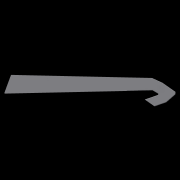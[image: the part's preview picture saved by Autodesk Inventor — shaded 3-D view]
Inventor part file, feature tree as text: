
AUTODESK INVENTOR PART (.ipt)
format: ipt  version: 2020 (Build 240168000, 168)  size: 9,527,808 bytes
history: native  units: in
note: dims shown in document units (in); Inventor stores cm internally (conversion verified against a paired STEP export)
features: other x166, extrude x71, fillet x44, projected_geometry x9, sketch x6, hole x4, loft x3, reference x2, plane x1, move_body x1
ambient origin geometry x8: Origin, YZ Plane, XZ Plane, XY Plane, X Axis, Y Axis, Z Axis, Center Point
bodies: Body (feature_tree), BodyFeature (feature_tree), BodyCut (feature_tree), BodyCutFeature (feature_tree), BodyCutFilletFeature (feature_tree), BodyCutCombineFeature (feature_tree), BodyCutEdgeFilletFeature (feature_tree), BodyRibFrontFilletsFeature (feature_tree), BodyBackRibFilletsFeature (feature_tree), BodyFretboardFilletsFeature (feature_tree), BodyFrontTopFilletsFeature (feature_tree), BodyFrontBottomFilletsFeature (feature_tree), BodyFrontNeckFilletsFeature (feature_tree), Solid22 (feature_tree), Solid23 (feature_tree), Solid62 (feature_tree), Solid64 (feature_tree), Solid65 (feature_tree), Solid68 (feature_tree), Solid50 (feature_tree), Solid52 (feature_tree), Solid54 (feature_tree), Solid56 (feature_tree), Solid57 (feature_tree), Solid59 (feature_tree)
feature tree (307):
  other  "MainBody"
  extrude  "NeckMountsProfileFeature"  Depth=0.5in TaperAngle=0.0deg
  other  "NeckPlane"
  extrude  "8StringFeature"  Depth=4.5in
  extrude  "6StringFeature"  Depth=1.12in
  extrude  "HornFeature"  Depth=0.6788in
  other  "6StringNeckFeature"
  other  "8StringNeckFeature"
  fillet  "InsideCornerFilletsFeature1/8"  Radius=0.6788in
  fillet  "OutsideFilletsFeature1/2"  Radius=0.125in
  fillet  "NeckMountOutsideFilletsFeature1/4"  Radius=0.5in
  fillet  "TipFilletsFeature1/8"  Radius=0.125in
  fillet  "BottomHornTipFilletFeature1/10"  Radius=0.1in
  fillet  "BottomHornFilletsFeature1/8"  Radius=0.125in
  fillet  "InsideHandleFilletsFeature1/2"  Radius=0.5in
  fillet  "InsideHandleFilletsFeature1/8"  Radius=0.125in
  fillet  "InsideTopHornFilletsFeature1/4"  Radius=0.25in
  fillet  "InsideTopHornFilletsFeature1/2"  Radius=0.5in
  fillet  "InsideBottomHornFilletsFeature1/4"  Radius=0.25in
  other  "PickupsOriginal"
  other  "MiddlePlane"
  other  "PickupsCustom"
  other  "PickupsModified"
  extrude  "TopPickupsIndentFeature"  Depth=0.0515in
  extrude  "BottomPickupsIndentFeature"  Depth=0.05in
  extrude  "TopPickupHolesFeature"  Depth=0.05in
  extrude  "BottomPickupHolesFeature"  Depth=0.05in
  fillet  "PickupIndentFilletsFeature"  Radius=5.7in
  other  "Frets"
  other  "FretsPreview"
  other  "TopHornHandleIndent"
  extrude  "TopHornBodyHandleFeature"  Depth=0.05in
  extrude  "TopHornHornHandleFeature"  Depth=0.05in
  other  "HornSculptFeature"
  other  "TopHornHandleFront"
  extrude  "TopHornHandleFrontFeature"  Depth=0.05in
  extrude  "TopHornHandleFront2Feature"  TaperAngle=45.0deg  [1 undecoded]
  extrude  "TopHornHandleFront3Feature"  TaperAngle=120.0deg  [1 undecoded]
  other  "TopHornHandleBack"
  extrude  "TopHornHandleBackFeature"  Depth=0.05in
  extrude  "TopHornHandleBack2Feature"  Depth=0.05in
  extrude  "TopHandleFeature"  Depth=0.05in
  extrude  "TopHandleFrontFeature"  Depth=0.05in
  extrude  "TopHandleBackFeature"  Depth=0.05in
  other  "Tuners"
  hole  "TunerHolesFeature"  [1 undecoded]
  other  "LogoMount"
  extrude  "LogoMountFeature"  Depth=0.05in
  other  "SideProfile"
  extrude  "SideProfileFeature"  Depth=0.05in
  other  "KeyboardCompartmentSidePlane"
  extrude  "KeyboardCompartmentFeature"  Depth=0.05in
  fillet  "KeyboardCompartmentFilletsFeature"  Radius=1.7in
  other  "ControlsBottom"
  other  "ControlsTop2"
  other  "ControlsTop1"
  extrude  "ControlsTop1Feature"  Depth=0.05in
  extrude  "ControlsTop2Feature"  Depth=0.05in
  extrude  "ControlsBottomFeature"  Depth=0.05in
  other  "HornSculptSideProfileFeature"
  fillet  "HornFretboardFilletFeature"  Radius=1.1in
  other  "ElectronicsCompartments"
  other  "InsideFacePlane1"
  other  "InsideFacePlane2"
  other  "InsideFacePlane3"
  extrude  "ElectronicCompartmentTopFeature"  Depth=0.05in
  extrude  "ElectronicCompartmentBottomFeature"  Depth=0.05in
  other  "ElectronicCompartmentsSculpt1Feature"
  other  "ElectronicCompartmentsSculpt2Feature"
  other  "ElectronicCompartmentsSculpt3Feature"
  other  "ElectronicCompartmentsSubtractFeature"
  extrude  "ElectronicCompartmentsSubtract2Feature"  Depth=0.05in
  fillet  "ElectronicCompartmentFillets1Feature"  Radius=1.277in
  fillet  "ElectronicCompartmentFillets2Feature"  Radius=1.277in
  extrude  "ControlIndentsBottomFeature"  Depth=0.05in
  fillet  "ElectronicCompartmentFillets3Feature"  Radius=1.0857in
  fillet  "ElectronicCompartmentFillets4Feature"  Radius=3.0in
  extrude  "ControlIndentsTopFeature"  Depth=0.05in
  other  "ControlIndents2Top"
  extrude  "ControlIndents2TopFeature"  Depth=0.05in
  fillet  "ControlIndents3FilletsFeature"  Radius=3.3665in
  extrude  "ControlIndents2RecutFeature"  Depth=0.05in
  fillet  "ElectronicCompartmentInsideFilletsFeature"  Radius=2.6in
  other  "BottomBridgePickupWirePlane"
  extrude  "BottomBridgePickupWireHoleFeature"  Depth=0.05in
  other  "BottomNeckPickupWirePlane"
  extrude  "BottomNeckPickupWireFeature"  Depth=0.05in
  extrude  "TopPickupWireFeature"  Depth=0.05in
  other  "SeaboardBlockCircuitboardMounts"
  extrude  "SeaboardBlockMountStemFeature"  Depth=0.05in
  extrude  "SeaboardBlockMountsFeature"  Depth=0.05in
  other  "SeaboardBlockKeyMounts"
  extrude  "SeaboardBlockKeyMountsFeature"  Depth=0.05in
  extrude  "SeaboardBlockRibbonsFeature"  Depth=0.05in
  extrude  "TunersTopFeature"  Depth=0.05in
  extrude  "TunersMiddleFeature"  Depth=0.05in
  extrude  "TunersBottomFeature"  Depth=0.05in
  fillet  "TunerFilletsFeature"  Radius=0.45in
  extrude  "NeckCutFeature"  Depth=0.05in
  fillet  "NeckCutFilletFeature"  Radius=1.481in
  other  "NeckCutCombineFeature"
  fillet  "NeckCutEdgeFilletFeature"  Radius=0.25in
  fillet  "NeckCutCornerFilletsFeature"  Radius=0.25in
  extrude  "NeckMountsFeature"  Depth=0.05in
  extrude  "FretMarkersTopFeature"  Depth=0.05in
  extrude  "FretMarkersBottomFeature"  TaperAngle=0.0deg  [1 undecoded]
  extrude  "FretsPreviewFeature"  Depth=0.3937in
  extrude  "FretLocksPreviewFeature"  Depth=0.05in
  hole  "FretLocksHolesFeature"  [1 undecoded]
  extrude  "TopHornHandleBodyFeature"  Depth=0.05in
  other  "TopHornSculpt3Feature"
  other  "TopHornSculpt4Feature"
  other  "TopHornSculpt5Feature"
  fillet  "TopHornHandleBodyFilletsFeature"  [1 undecoded]
  fillet  "TopHornHandleFilletsFeature"  [1 undecoded]
  other  "TopHornAdjustFeature"
  fillet  "TopHornAdjustFilletFeature"  Radius=26.75in
  other  "HandlePlane1"
  other  "HandlePlane2"
  other  "Handle"
  extrude  "HandleBackFeature"  Depth=0.05in
  extrude  "HandleFrontFeature"  Depth=0.05in
  other  "HandleSculpt1Feature"
  other  "HandleSculpt2Feature"
  other  "HandleSculpt3Feature"
  other  "HandleSculpt4Feature"
  other  "HandleSculpt5Feature"
  other  "HandleSculpt6Feature"
  other  "HandleEdit1Feature"
  other  "HandleEdit2Feature"
  fillet  "HandleBodyFilletsFeature"  Radius=0.3333in
  fillet  "HandleRibFilletsFeature"  Radius=0.333in
  other  "HornBackSculptFeature"
  other  "HornHandleBackSculpt1Feature"
  other  "HornHandleBackSculpt2Feature"
  fillet  "HornHandleackSculptFilletsFeature"  Radius=0.1in
  fillet  "HandleMeshFilletsFeature"  Radius=0.1in
  fillet  "HornMeshFillets1Feature"  [1 undecoded]
  fillet  "FretboardEndFilletsFeature"  Radius=0.1in
  other  "KeyboardCompartmentSideProfile"
  extrude  "KeyboardCompartmentExactFeature"  Depth=0.05in
  extrude  "KeyboardCompartmentSideFeature"  Depth=0.05in
  other  "KeyboardCompartmentExactSubtractFeature"
  other  "8NeckSplitFeature"
  other  "8NeckLoftStartPlane"
  other  "8NeckLoftEndPlane"
  loft  "8NeckLoftFeature"
  other  "6NeckSplitForLoftFeature"
  other  "6NeckLoftEndPlane"
  other  "6NeckLoftStartPlane"
  extrude  "OscScreenFeature"  Depth=0.05in
  other  "OscCompartmentPlane"
  other  "OscIndentPlane"
  extrude  "OscCompartmentFeature"  Depth=0.05in
  other  "OscCompartmentSubtractFeature"
  extrude  "OscMountFeature"  Depth=0.05in
  other  "OscCoverIndentPlane"
  extrude  "OscCoverIndentFeature"  TaperAngle=0.0deg  [1 undecoded]
  fillet  "OscCoverIndentFilletsFeature"  Radius=0.25in
  extrude  "OscCoverMountHolesFeature"  Depth=0.05in TaperAngle=0.0deg
  fillet  "ElectronicCompartmentLastFilletFeature"  Radius=0.2in
  loft  "6NeckLoftFeature"
  extrude  "6CloseCutFeature"  Depth=0.05in
  other  "HeadSculpt1Feature"
  other  "HeadThickness"
  other  "HeadSculpt2Feature"
  other  "HeadSculpt3Plane"
  extrude  "HeadSculpt3Feature"  Depth=0.05in
  other  "HeadSculpt4Feature"
  other  "8HeadCombineFeature"
  other  "8HeadCleanupFeature"
  fillet  "8HeadFilletFeature"  Radius=0.5333in
  other  "HeadSculpt5Plane"
  other  "HeadSculpt5Feature"
  other  "HeadSculpt6Feature"
  other  "HeadSculpt7Plane"
  extrude  "HeadSculpt7Feature"  Depth=0.05in
  other  "6StringCombineFeature"
  other  "6NeckFilletSplitFeature"
  other  "8NeckFilletSplitFeature"
  fillet  "InsideHeadFilletFeature"  Radius=0.5in
  other  "CombineFilletsFeature"
  fillet  "HornHeadFilletsFeature"  Radius=5.55in
  fillet  "HornFillet3Feature"  Radius=1.75in
  other  "HornFinalSplitFeature"
  other  "6FinalSplitFeature"
  other  "6CombineFeature"
  other  "8NeckJoin"
  other  "6NeckJoin"
  extrude  "8NeckJoinFeature"  Depth=0.05in
  fillet  "8NeckJoinFilletFeature"  Radius=0.1in
  extrude  "6NeckJoinFeature"  TaperAngle=0.0deg  [1 undecoded]
  extrude  "SeaboardBlockMountHolesFeature"  Depth=0.05in
  extrude  "PickupRecutFeature"  Depth=0.3937in
  extrude  "BackCoverIndentFeature"  Depth=0.05in
  extrude  "ElectronicsCompartmentSupportFeature"  Depth=0.05in
  fillet  "ElectronicsCompartmentSupportFilletsFeature"  Radius=0.2in
  hole  "BackCoverMountsFeature"  [1 undecoded]
  other  "OscCoverBottom"
  other  "OscCoverTopPlane"
  other  "OscCoverMounts"
  loft  "OscCoverFeature"
  extrude  "OscCoverBodyCutFeature"  Depth=0.05in TaperAngle=0.0deg
  fillet  "OscCoverBodyCutFilletsFeature"  Radius=0.125in
  other  "OscCoverBodyCutSubtractFeature"
  fillet  "OscCoverBodyFilletFeature"  Radius=0.1in
  extrude  "OscCoverMountsFeature"  Depth=0.05in
  extrude  "LogoCompartmentFeature"  Depth=0.05in
  other  "LogoMounts"
  extrude  "LogoMountsFeature"  Depth=0.05in
  fillet  "LogoMountsFilletsFeature"  Radius=0.25in
  hole  "LogoMountHolesFeature"  [1 undecoded]
  extrude  "Extrusion179"  Depth=0.05in
  other  "KeyboardCompartment"
  other  "TopHandle"
  other  "TunerLocksBody"
  other  "FretsBody"
  other  "TunersTop"
  other  "TunersMiddle"
  other  "TunersBottom"
  other  "ElectronicCompartments1Body"
  other  "NeckCut"
  other  "NeckMounts"
  other  "TopHornHandle"
  other  "TopHornHandleBody"
  projected_geometry  "Projected Loop22"
  projected_geometry  "Projected Loop23"
  other  "TopHandleFront"
  projected_geometry  "Projected Loop24"
  other  "TopHandleBack"
  other  "HandleBody"
  other  "TopHornSculpt3Plane"
  other  "TopHornSculpt4Plane"
  other  "TopHornSculpt5Plane"
  other  "HandleSculpt1Plane"
  other  "HandleSculpt2Plane"
  other  "HandleSculpt3Plane"
  other  "HandleSculpt4Plane"
  other  "HandleSculpt5Plane"
  other  "HandleSculpt6Plane"
  other  "HornBody"
  other  "8StringBody"
  other  "6StringBody"
  other  "NeckMountsProfile"
  other  "HornBackSculptPlane"
  other  "HornSculptFrontPlane"
  plane  "Work Plane62"
  other  "8NeckStartProfile"
  other  "8NeckEndProfile"
  sketch  "Sketch127"  dims[d8=0.7696in d18=0.5in d119=1.75in d120=0.0in]
  other  "6NeckLoftStartProfile"
  other  "6NeckLoftEndProfile"
  projected_geometry  "Projected Loop27"
  other  "6CloseCut"
  sketch  "Sketch131"  dims[d433=1.0857in d464=4.5in d466=0.25in]
  other  "HeadSculpt1Plane"
  other  "HeadSculpt2Plane"
  other  "HeadSculpt3Profile"
  other  "HeadSculpt4Plane"
  other  "HeadSculpt7Profile"
  other  "6NeckFilletSplit"
  other  "8NeckFilletSplit"
  sketch  "Sketch138"  dims[d501=0.25in d582=1.12in]
  sketch  "Sketch139"  dims[d644=25.0in d654=0.6788in d681=0.6788in d700=0.125in d702=0.5in d703=0.125in d705=0.1in d706=0.125in d707=0.5in d708=0.125in d709=0.25in d710=0.5in d711=0.25in]
  other  "ControlIndentsBottom"
  other  "BottomBridgePickupWireHole"
  other  "BottomNeckPickupWire"
  other  "TopPickupWire"
  other  "HornHandleBackSculpt1Plane"
  other  "HornHandleBackSculpt2Plane"
  sketch  "Sketch165"  dims[d716=2.2835in d717=0.0515in]
  other  "OscScreen"
  other  "OscCompartment"
  other  "OscMount"
  other  "OscCoverPlane"
  other  "OscCoverIndent"
  other  "OscCoverMountHoles"
  projected_geometry  "Projected Loop32"
  other  "KeyboardCompartmentExact"
  projected_geometry  "Projected Loop35"
  other  "SeaboardBlockMountHoles"
  reference  "Reference6"
  reference  "Reference7"
  other  "PickupRecut"
  other  "BackCoverIndent"
  other  "ElectronicsCompartmentSupport"
  other  "BackCoverMounts"
  other  "OscCoverTop"
  other  "OscCoverBody"
  other  "LogoCompartment"
  sketch  "Sketch206"  dims[d718=13.825in d719=0.213in d721=0.9414in d722=1.1649in d724=5.7in d725=7.5379in d726=0.2542in d727=2.0in d728=45.0deg d729=120.0deg d730=0.3642in d731=0.9371in d745=5.6289in d747=6.0in d748=4.3in d750=0.8658in d751=0.6506in d753=0.4054in d754=0.8in d779=0.101in d781=1.7in d782=7.125in d783=2.6in d784=0.933in d787=1.1in d792=3.625in d793=4.0in d819=3.5in d825=1.277in d834=1.277in d836=1.5in d837=1.0857in d838=3.0in d839=2.0in d841=4.5in d846=3.3665in d850=0.1512in d853=2.6in d864=1.5757in d961=0.5in d962=0.5in d963=0.3779in d964=0.3779in d965=0.45in d966=0.45in d967=0.8795in d968=1.1386in d969=1.1386in d970=0.45in d971=4.009in d972=1.481in d979=0.25in d980=0.25in d982=0.1718in d983=0.1718in d984=0.0in d985=0.7874in d987=4.0in d988=0.3937in d990=1.0in d994=2.746in d995=1.481in d996=0.9256in d999=0.0in d1000=0.0in d1022=26.75in d1023=28.0in d1024=25.5in d1026=0.3333in d1041=0.333in d1042=0.1in d1044=0.1in d1048=0.0in d1049=0.0in d1054=0.1in d1055=0.1in d1057=0.748in d1060=0.0in d1061=0.0in d1064=0.4662in d1092=0.7in d1095=1.7in d1100=0.0in d1101=0.0in d1117=0.25in d1118=0.0in d1119=0.3in d1120=0.0in d1122=0.2in d1123=0.0in d1277=0.6459in d1329=0.5333in d1334=0.333in d1335=0.5333in d1339=0.125in d1348=0.5in d1358=5.55in d1359=1.75in d1373=0.2in d1375=0.1in d1376=0.0in d1406=1.125in d1430=3.1496in d1432=0.525in d1433=0.3937in d1435=1.0in d1439=1.8in d1440=1.125in d1441=0.2in d1475=0.1in d1476=0.75in d1477=0.375in d1478=0.25in d1479=0.5635in d1480=0.5in d1481=0.8108in d1483=0.05in d1484=0.0in d1485=0.05in d1486=0.0in d1487=0.05in d1488=0.0in d1489=0.125in d1490=0.1in d1491=2.846in d1492=1.481in d1493=0.5in d1494=0.25in d1496=0.1in d1504=0.13in d1508=0.1in d1511=3.063in d1512=0.1295in d1513=0.1295in d1526=0.5708in d1527=0.1286in d1528=1.3799in d1529=1.3958in d1530=1.1055in d1531=0.8208in d1534=2.3622in d1536=0.45in d1537=0.3937in d1539=1.0in d1574=1.0in d1575=0.0in d1576=0.0in d1577=0.4789in d1578=0.4308in d1579=1.1471in d1580=2.5in d1581=1.275in d1582=1.1845in d1583=1.481in d1584=1.1384in d1585=0.7644in d1586=2.746in d1587=0.264in d1588=0.4in d1589=0.0in d1590=0.75in d1591=0.0in d1592=1.0in d1593=0.0in d1594=1.0in d1595=0.0in d1596=0.144in d1597=3.75in d1598=0.1295in d1599=0.1295in d1638=10.0in d1639=14.2465in d1641=11.25in d1648=0.5in d1649=0.0in d1650=28.0in d1657=1.0in d1659=5.5in d1660=4.25in d1662=0.3333in d1663=0.0in d1664=10.0in d1665=1.0in d1671=0.1in d1672=0.5in d1676=3.0in d1677=2.425in d1682=0.75in d1683=0.0in d1690=1.1878in d1691=0.9817in d1692=1.0844in d1693=0.8784in d1695=0.2in d1696=0.0in d1750=1.525in d1751=0.0in d1752=0.5in d1777=0.5in d1778=0.0in d1779=0.5in d1780=0.0in d1781=0.5in d1782=0.0in d1783=0.6in d1784=0.0in d1790=0.65in d1791=0.0in d1792=0.65in d1793=0.0in d1795=0.125in d1821=0.1in d1828=0.0in d1829=0.0in d1830=0.475in d1831=0.125in d1832=0.125in d1843=3.0403in d1844=2.1333in d1845=0.758in d1847=1.75in d1848=0.0in d1849=1.9in d1850=0.0in d1851=1.9in d1852=0.0in d1858=0.9in d1859=0.0in d1862=0.0in d1863=0.0in d1864=0.5in d1865=0.0in d1866=0.5in d1867=0.0in d1870=0.2056in d1871=0.257in d1872=0.0674in d1875=0.25in d1876=0.0in d1877=0.15in d1880=0.15in d1882=0.05in d1883=0.05in d1885=1.3537in d1887=10.0in d1888=0.1in d1889=0.1in d1890=20.0in d1891=20.0in d1894=0.0618in d1900=0.1in d1901=0.4524in d1903=0.006in d1904=0.0in d1915=0.22in d1921=0.0in d1922=90.0deg d1923=0.0in d1924=90.0deg d1925=1.2in d1926=0.7in d1927=0.3333in d1928=0.001in d1929=0.25in d1930=1.25in d1931=0.25in d1935=0.8in d1936=0.3489in d1937=0.22in d1938=0.25in d1939=0.5in d1940=0.6in d1941=0.15in d1942=0.4in d1943=0.0in d1944=90.0deg d1945=0.0in d1946=90.0deg d1948=1.3333in d1949=2.125in d1951=1.125in d1952=2.55in d1957=3.0in d1958=0.1in d1959=0.1in d1960=0.1in d1961=1.0in d1962=0.0in d1966=1.0in d1967=0.0in d1968=0.44in d1969=0.0in d1975=0.1in d1976=0.1in d1980=10.6875in d1981=5.1875in d1982=0.85in d1983=0.3333in d1985=7.5816in d1987=0.1in d1988=0.0in d1989=0.1875in d1990=0.5333in d1992=150.0deg d1993=3.25in d1996=-0.325in d1997=-0.125in d1998=1.0in d1999=0.0in d2004=0.5in d2005=0.0in d2007=0.0938in d2008=0.5in d2009=0.25in d2010=2.3125in d2011=0.7188in d2015=0.25in d2016=5.0in d2019=0.125in d2020=0.25in d2027=0.2in d2028=0.0in d2029=0.02in d2030=0.0in d2039=0.55in d2047=0.25in d2048=0.25in d2049=0.0in d2050=0.0in d2052=2.295in d2053=0.0in d2056=0.25in d2058=0.25in d2059=0.3333in d2060=0.3333in d2061=0.25in d2062=0.3333in d2063=0.3333in d2064=0.0in d2065=0.0in d2066=0.339in d2067=0.1643in d2068=0.1in d2069=0.1in d2070=0.1in d2071=0.1in d2072=0.1643in d2073=0.1643in d2074=0.1643in d2077=3.3125in d2078=3.313in d2079=0.305in d2080=0.3333in d2081=1.0in d2082=0.0in d2083=0.3333in d2084=0.0in d2086=0.719in d2087=2.3125in d2088=0.125in d2089=0.1in d2090=0.438in d2091=0.438in d2092=0.438in d2093=0.438in d2094=0.25in d2095=0.0in d2096=0.25in d2097=0.25in d2098=2.0in d2100=2.5in d2102=0.75in d2103=0.25in d2104=0.25in d2105=0.0in d2106=0.625in d2111=10.0in d2112=0.125in d2113=0.3333in d2117=1.75in d2118=1.25in d2119=1.625in d2120=0.25in d2121=1.0in d2122=0.1in d2125=0.7in d2132=1.625in d2133=1.0in d2134=0.1in d2135=1.0in d2136=1.0in d2137=0.1in d2138=1.025in d2139=1.025in d2140=0.5in d2141=0.7in d2142=1.075in d2143=0.7in d2144=0.5in d2146=0.25in d2147=0.25in d2148=0.5in d2149=1.75in d2150=0.0in d2151=0.0in d2152=0.035in d2153=0.0in d2154=0.0in d2155=0.0in d2156=-0.325in d2157=1.0in d2158=0.2in d2159=0.0in d2160=1.0in d2161=0.2in d2162=0.0in d2164=1.0in d2165=2.2612in d2166=0.605in d2167=0.01in d2168=0.3333in d2169=0.5388in d2170=0.4in d2171=2.625in d2172=1.375in d2173=0.172in d2174=0.281in d2175=0.5in d2176=0.0in d2177=-2.0in d2178=1.797in d2179=0.0in d2180=-0.125in d2181=0.06in d2182=0.06in d2183=0.505in d2184=0.9375in d2185=2.625in d2186=1.375in d2187=2.5in d2188=1.0313in d2189=0.05in d2190=0.1719in d2191=0.0625in d2192=0.0625in d2193=0.1094in d2194=0.0312in d2195=0.0312in d2196=0.0312in d2197=0.0312in d2198=0.0312in d2199=0.0312in d2200=0.0312in d2201=0.0312in d2202=0.203in d2203=0.0in d2207=-0.2in d2211=0.15in d2212=1.0in d2213=0.0in d2214=0.15in d2215=0.15in d2216=0.1in d2220=0.05in d2221=1.5in d2222=0.0in d2230=0.6836in d2238=1.0in d2239=0.25in d2240=0.1in d2241=0.0689in d2243=1.1408in d2244=0.449in d2245=1.6223in d2246=2.1038in d2247=0.449in d2248=0.0463in d2249=0.4549in d2251=0.3908in d2252=0.3908in d2255=0.8in d2257=3.5in d2259=1.1973in d2261=0.625in d2262=0.625in d2263=0.536in d2264=2.7in d2265=0.25in d2266=0.2in d2267=0.0in d2268=0.2in d2269=0.0in d2278=0.4264in d2279=1.0in d2280=0.0in d2281=21.986in d2282=0.0in d2283=0.1in d2284=0.1in d2285=0.5in d2286=0.0in d2287=0.5333in d2288=0.1in d2293=0.85in d2294=1.0in d2295=0.25in d2296=0.749in d2297=0.0in d2298=0.25in d2299=0.1984in d2300=0.1in d2301=0.0in d2302=0.2in d2303=0.0in d2304=0.481in d2305=0.481in d2306=0.5in d2307=0.25in d2308=0.1in d2309=0.75in d2310=0.375in d2311=0.25in d2312=0.5635in d2313=0.5in d2314=0.8108in d2319=0.0in d2320=0.0in d2321=90.0deg d2322=0.0in d2323=90.0deg d2324=0.5in d2325=0.0in d2326=28.0in d2327=1.0in d2328=1.5in d2329=0.0in d2330=0.2in d2331=0.2in d2333=0.22in d2335=0.12in d2336=0.12in d2337=0.1in d2338=0.1in d2339=0.75in d2340=0.375in d2341=0.25in d2342=0.5635in d2343=0.5in d2344=0.8108in d2347=0.25in d2348=0.3in d2349=0.15in d2350=0.15in d2351=0.3in d2352=0.15in d2353=0.3in d2354=0.25in d2355=0.25in d2356=0.25in d2357=0.25in d2358=0.25in d2359=0.1958in d2360=0.1958in d2361=0.1in d2362=0.1in d2363=0.1in d2364=0.1in d2365=0.2in d2366=0.0in d2369=0.3333in d2370=0.0in d2371=0.05in d2372=0.05in d2373=0.75in d2374=0.375in d2375=0.25in d2376=0.5635in d2377=1.0in d2378=0.8108in d2379=1.05in d2380=0.0in d2381=0.7in d2382=0.6in d620=0.5in d621=0.0344in d622=0.5in d623=0.0344in d1625=0.5in d1626=0.0344in d1627=0.5in d1628=0.0344in d1730=0.5in d1731=0.0344in d1732=0.5in d1733=0.0344in d1822=0.5in d1823=0.0344in d1824=0.5in d1825=0.0344in d1837=0.5in d1838=0.0344in d1839=0.5in d1840=0.0344in d1860=0.5in d1861=0.0344in d1947=0.5in d1950=0.0344in d2012=0.5in d2013=0.0344in d2101=0.5in]
  projected_geometry  "Projected Loop40"
  projected_geometry  "Projected Loop41"
  projected_geometry  "Projected Loop42"
  other  "Delete13"
  move_body  "Move3"
  other  "Delete14"
  other  "6StringNeckCombineBody"
  other  "8StringNeckBody"
  other  "6StringNeckBody"
  other  "TopHornBody"
  other  "8StringCombinedBody"
  other  "6StringCombinedBody"
  other  "Delete18"
  other  "<userpath>\Desktop\switchback\src\switchback-exploded.iam"
  other  "switchback-exploded.iam"
  other  "seaboard-block-keyboard:1"
note: 12 required parameter values undecoded (feature->parameter linkage not recoverable at this tier; creation-order binding heuristic only, values carry confidence <= 0.55)
